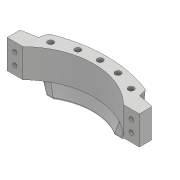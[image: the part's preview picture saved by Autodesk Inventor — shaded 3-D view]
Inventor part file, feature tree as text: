
AUTODESK INVENTOR PART (.ipt)
format: ipt  version: 2017 (Build 210142000, 142)  size: 522,752 bytes
history: native  units: mm
features: sketch x16, loft x7, plane x3, fillet x3, extrude x2
ambient origin geometry x8: Origin, YZ Plane, XZ Plane, XY Plane, X Axis, Y Axis, Z Axis, Center Point
bodies: Body1 (feature_tree)
feature tree (31):
  sketch  "Sketch1"  dims[d0=11.0mm d1=9.0mm]
  plane  "Work Plane1"
  loft  "Loft1"
  sketch  "Sketch3"  dims[d8=11.0mm d9=9.0mm]
  plane  "Work Plane2"
  loft  "Loft2"
  fillet  "Fillet1"  Radius=6.0mm
  fillet  "Fillet2"  Radius=20.071286mm
  fillet  "Fillet3"  Radius=70.0mm
  loft  "Loft3"
  loft  "Loft4"
  loft  "Loft5"
  loft  "Loft6"
  loft  "Loft7"
  sketch  "Sketch15"  dims[d30=17.453293mm]
  plane  "Work Plane3"
  extrude  "Extrusion4"  Depth=11.0mm
  extrude  "Extrusion5"  Depth=11.0mm
  sketch  "Sketch2"  dims[d2=11.0mm d3=17.453293mm d4=6.0mm d5=20.071286mm d6=70.0mm]
  sketch  "Sketch4"  dims[d10=11.0mm d11=17.453293mm]
  sketch  "Sketch5"  dims[d12=6.0mm d13=20.071286mm]
  sketch  "Sketch6"  dims[d14=90.0mm d15=50.0mm]
  sketch  "Sketch7"  dims[d19=11.0mm d20=70.0mm]
  sketch  "Sketch8"  dims[d21=50.0mm d22=11.0mm]
  sketch  "Sketch9"  dims[d23=9.0mm d24=11.0mm]
  sketch  "Sketch10"  dims[d25=17.453293mm]
  sketch  "Sketch11"  dims[d26=3.0mm]
  sketch  "Sketch12"  dims[d27=20.071286mm]
  sketch  "Sketch13"  dims[d28=9.0mm]
  sketch  "Sketch14"  dims[d29=11.0mm]
  sketch  "Sketch17"  dims[d31=3.0mm d32=20.071286mm d33=105.0mm d34=0.0mm d35=90.0deg d36=0.0mm d37=90.0deg d38=7.0mm d39=14.835299mm d40=50.01168mm d41=59.999995mm d42=105.0mm d43=7.0mm d44=16.580628mm d45=9.0mm d46=6.0mm d47=8.0mm d48=60.0deg d49=42.0mm d50=40.0mm d51=6.0mm d52=8.0mm d53=60.0deg d54=80.0mm d55=0.0mm d56=90.0deg d57=0.0mm d58=90.0deg d59=3.0mm d60=1.0mm d61=1.0mm d62=3.0mm d63=4.0mm d64=0.0mm d65=90.0deg d66=0.0mm d67=90.0deg d68=3.0mm d69=4.0mm d70=0.0mm d71=90.0deg d72=0.0mm d73=90.0deg d74=3.0mm d75=4.0mm d76=0.0mm d77=90.0deg d78=0.0mm d79=90.0deg d80=3.0mm d81=4.0mm d82=0.0mm d83=90.0deg d84=0.0mm d85=90.0deg d86=3.0mm d87=4.0mm d88=0.0mm d89=90.0deg d90=0.0mm d91=90.0deg d92=3.0mm d93=3.0mm d94=3.0mm d98=-5.0mm d105=3.0mm d106=10.0mm d107=0.0mm d108=6.5mm d109=6.5mm d110=6.5mm d111=6.5mm d112=10.0mm d113=0.0mm]
